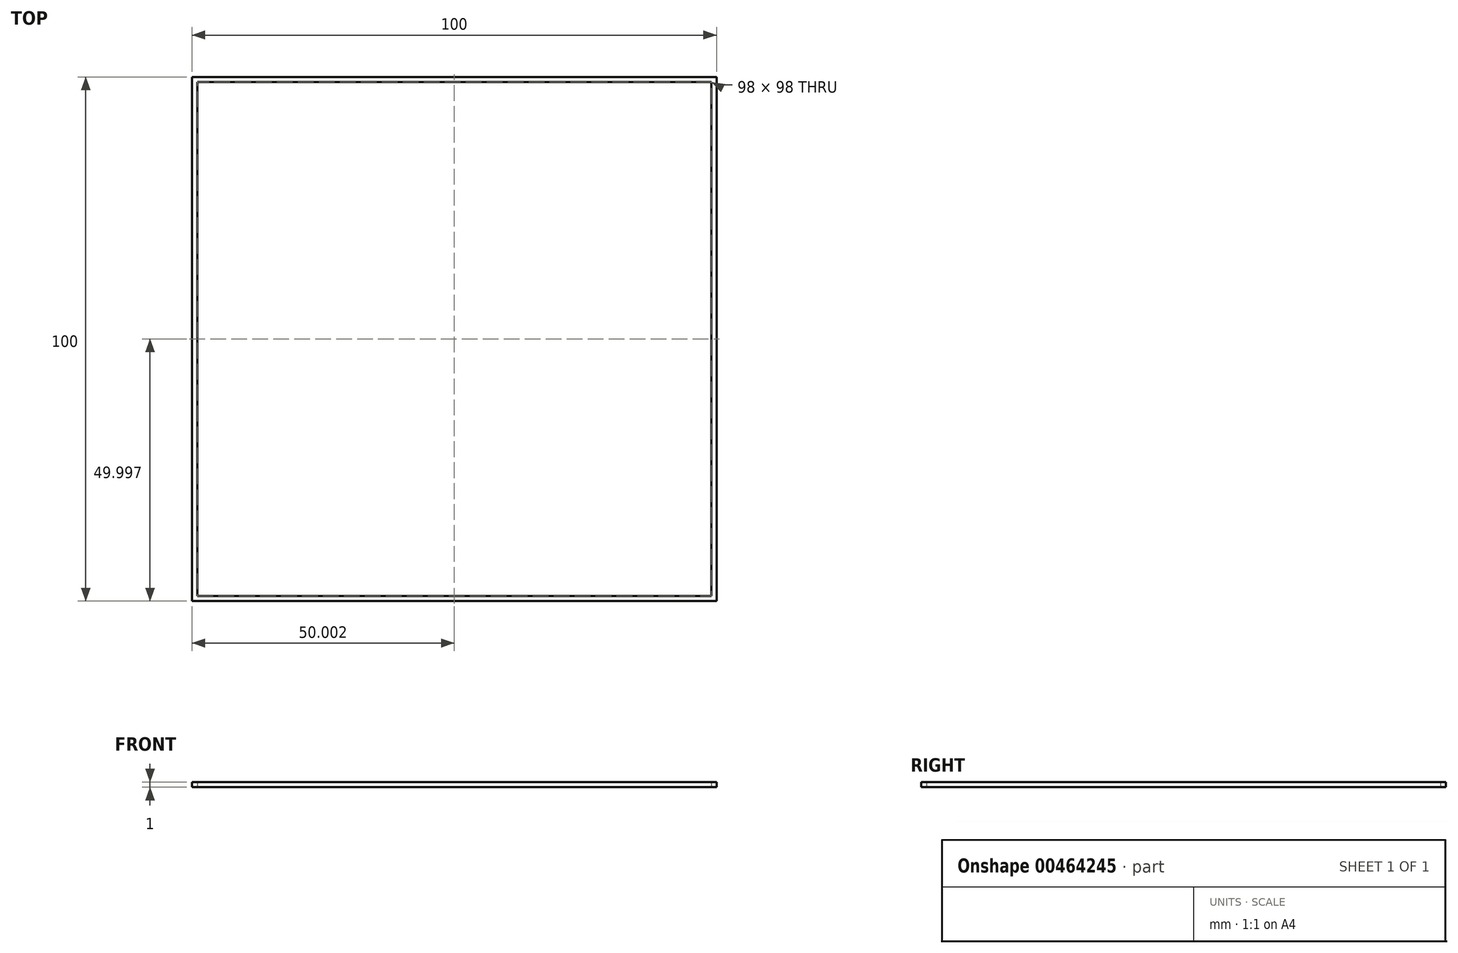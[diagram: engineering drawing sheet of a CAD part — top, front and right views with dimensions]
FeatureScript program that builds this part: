
annotation { "Feature Type Name" : "Feature", "Feature Type Description" : "" }
export const myFeature = defineFeature(function(context is Context, id is Id, definition is map)
    precondition{}
    {
        {
            var Q0;
            Q0=qCreatedBy(makeId("Top.planeOp"),FACE);
            var sketch = newSketch(context, id + "F0", { "sketchPlane" : qUnion([Q0])});
            skLineSegment(sketch, "E0.bottom", {"start": v(-48.68, 53.38) * mm, "end": v(51.32, 53.38) * mm});
            skLineSegment(sketch, "E0.top", {"start": v(-48.68, -46.62) * mm, "end": v(51.32, -46.62) * mm});
            skLineSegment(sketch, "E0.left", {"start": v(-48.68, 53.38) * mm, "end": v(-48.68, -46.62) * mm});
            skLineSegment(sketch, "E0.right", {"start": v(51.32, 53.38) * mm, "end": v(51.32, -46.62) * mm});
            skLineSegment(sketch, "E1.bottom", {"start": v(-47.68, 52.38) * mm, "end": v(50.32, 52.38) * mm});
            skLineSegment(sketch, "E1.top", {"start": v(-47.68, -45.62) * mm, "end": v(50.32, -45.62) * mm});
            skLineSegment(sketch, "E1.left", {"start": v(-47.68, 52.38) * mm, "end": v(-47.68, -45.62) * mm});
            skLineSegment(sketch, "E1.right", {"start": v(50.32, 52.38) * mm, "end": v(50.32, -45.62) * mm});
            skSolve(sketch);
        }
        {
            var Q0;
            Q0=makeQuery(id+"F0.imprint","IMPRINT",FACE,{"disambiguationData":[TD([[makeQuery(id+"F0.imprint","IMPRINT",EDGE,{"derivedFrom":sQuery(id+"F0.wireOp",EDGE,"E0.bottom")}),-1.0]])]});
            extrude(context, id + "F1", {"entities" : qUnion([Q0]), "depth" : 1 * mm});
        }
    });
